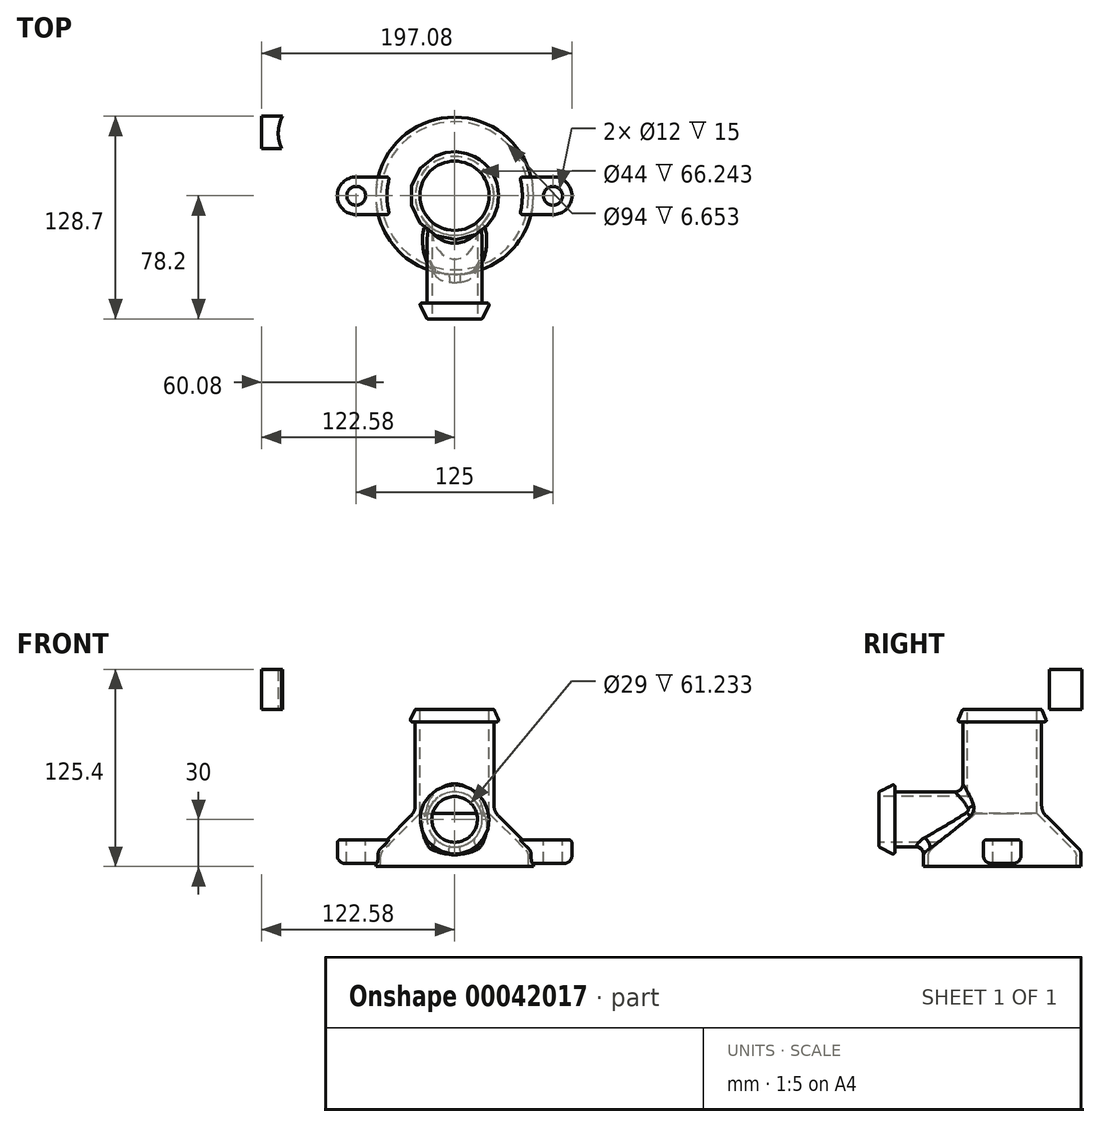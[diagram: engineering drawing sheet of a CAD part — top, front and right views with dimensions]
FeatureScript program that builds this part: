
annotation { "Feature Type Name" : "Feature", "Feature Type Description" : "" }
export const myFeature = defineFeature(function(context is Context, id is Id, definition is map)
    precondition{}
    {
        {
            var Q0;
            Q0=qCreatedBy(makeId("Front.planeOp"),FACE);
            var sketch = newSketch(context, id + "F0", { "sketchPlane" : qUnion([Q0])});
            skLineSegment(sketch, "E0", {"start": v(0, 100) * mm, "end": v(0, 0) * mm});
            skLineSegment(sketch, "E1", {"start": v(0, 0) * mm, "end": v(50, 0) * mm});
            skLineSegment(sketch, "E2", {"start": v(50, 0) * mm, "end": v(50, 10) * mm});
            skLineSegment(sketch, "E3", {"start": v(50, 10) * mm, "end": v(25, 35) * mm});
            skLineSegment(sketch, "E4", {"start": v(25, 35) * mm, "end": v(25, 92) * mm});
            skLineSegment(sketch, "E5", {"start": v(25, 92) * mm, "end": v(28.5, 92) * mm});
            skLineSegment(sketch, "E6", {"start": v(28.5, 92) * mm, "end": v(25, 100) * mm});
            skLineSegment(sketch, "E7", {"start": v(25, 100) * mm, "end": v(0, 100) * mm});
            skLineSegment(sketch, "E8", {"start": v(25, 100) * mm, "end": v(25, 92) * mm});
            skSolve(sketch);
        }
        {
            var Q0;
            Q0=qCreatedBy(makeId("Right.planeOp"),FACE);
            var sketch = newSketch(context, id + "F1", { "sketchPlane" : qUnion([Q0])});
            skLineSegment(sketch, "E9", {"start": v(0, 0) * mm, "end": v(96.43, 0) * mm, "construction": true});
            skLineSegment(sketch, "E10", {"start": v(0, 0) * mm, "end": v(0, 117.17) * mm, "construction": true});
            skLineSegment(sketch, "E11", {"start": v(0, 47.5) * mm, "end": v(-68.2, 47.5) * mm});
            skLineSegment(sketch, "E12", {"start": v(-68.2, 47.5) * mm, "end": v(-68.2, 52.5) * mm});
            skLineSegment(sketch, "E13", {"start": v(-68.2, 52.5) * mm, "end": v(-78.2, 47.5) * mm});
            skLineSegment(sketch, "E14", {"start": v(-78.2, 47.5) * mm, "end": v(-78.2, 30) * mm});
            skLineSegment(sketch, "E15", {"start": v(-78.2, 30) * mm, "end": v(0, 30) * mm});
            skLineSegment(sketch, "E16", {"start": v(0, 30) * mm, "end": v(0, 47.5) * mm});
            skLineSegment(sketch, "E17", {"start": v(-68.2, 47.5) * mm, "end": v(-78.2, 47.5) * mm});
            skLineSegment(sketch, "E18", {"start": v(0, 30) * mm, "end": v(-77.9, 30) * mm, "construction": true});
            skSolve(sketch);
        }
        {
            var Q0;
            Q0=makeQuery(id+"F0.imprint","IMPRINT",FACE,{"disambiguationData":[TD([[makeQuery(id+"F0.imprint","IMPRINT",EDGE,{"derivedFrom":sQuery(id+"F0.wireOp",EDGE,"E0")}),1.0]])]});
            var Q1;
            Q1=sQuery(id+"F0.wireOp",EDGE,"E6");
            var Q2;
            Q2=sQuery(id+"F0.wireOp",EDGE,"E5");
            var Q3;
            Q3=sQuery(id+"F0.wireOp",EDGE,"E4");
            var Q4;
            Q4=sQuery(id+"F0.wireOp",EDGE,"E3");
            var Q5;
            Q5=sQuery(id+"F0.wireOp",EDGE,"E2");
            var Q6;
            Q6=sQuery(id+"F0.wireOp",EDGE,"E0");
            revolve(context, id + "F2", {"entities" : qUnion([Q0]), "surfaceEntities" : qUnion([Q1, Q2, Q3, Q4, Q5]), "axis" : qUnion([Q6]), "revolveType" : RevolveType.FULL});
        }
        {
            var Q0;
            Q0=makeQuery(id+"F1.imprint","IMPRINT",FACE,{"disambiguationData":[TD([[makeQuery(id+"F1.imprint","IMPRINT",EDGE,{"derivedFrom":sQuery(id+"F1.wireOp",EDGE,"E11")}),1.0]])]});
            var Q1;
            Q1=sQuery(id+"F1.wireOp",EDGE,"E15");
            revolve(context, id + "F3", {"operationType" : NewBodyOperationType.ADD, "entities" : qUnion([Q0]), "axis" : qUnion([Q1]), "revolveType" : RevolveType.FULL});
        }
        {
            var Q0;
            Q0=makeQuery(id+"F2.opRevolve","SWEPT_FACE",FACE,{"disambiguationData":[OSD([sQuery(id+"F0.wireOp",EDGE,"E7")])]});
            var Q1;
            Q1=makeQuery(id+"F2.opRevolve","SWEPT_FACE",FACE,{"disambiguationData":[OSD([sQuery(id+"F0.wireOp",EDGE,"E1")])]});
            var Q2;
            Q2=makeQuery(id+"F3.opRevolve","SWEPT_FACE",FACE,{"disambiguationData":[OSD([sQuery(id+"F1.wireOp",EDGE,"E14")])]});
            shell(context, id + "F4", {"entities" : qUnion([Q0, Q1, Q2]), "thickness" : 3 * mm});
        }
        {
            var Q0;
            Q0=makeQuery(id+"F0.imprint","IMPRINT",FACE,{"disambiguationData":[TD([[makeQuery(id+"F0.imprint","IMPRINT",EDGE,{"derivedFrom":sQuery(id+"F0.wireOp",EDGE,"E5")}),1.0]])]});
            var Q1;
            Q1=makeQuery(id+"F4.opShell","OFFSET_FACE",FACE,{"disambiguationData":[OSD([sQuery(id+"F0.wireOp",EDGE,"E4"),sQuery(id+"F0.wireOp",EDGE,"E8")])]});
            revolve(context, id + "F5", {"operationType" : NewBodyOperationType.ADD, "entities" : qUnion([Q0]), "axis" : qUnion([Q1]), "revolveType" : RevolveType.FULL});
        }
        {
            var Q0;
            Q0=makeQuery(id+"F1.imprint","IMPRINT",FACE,{"disambiguationData":[TD([[makeQuery(id+"F1.imprint","IMPRINT",EDGE,{"derivedFrom":sQuery(id+"F1.wireOp",EDGE,"E12")}),1.0]])]});
            var Q1;
            Q1=makeQuery(id+"F3.opRevolve","SWEPT_FACE",FACE,{"disambiguationData":[OSD([sQuery(id+"F1.wireOp",EDGE,"E11"),sQuery(id+"F1.wireOp",EDGE,"E17")])]});
            revolve(context, id + "F6", {"operationType" : NewBodyOperationType.ADD, "entities" : qUnion([Q0]), "axis" : qUnion([Q1]), "revolveType" : RevolveType.FULL});
        }
        {
            var Q0;
            Q0=makeQuery(id+"F2.opRevolve","SWEPT_FACE",FACE,{"disambiguationData":[OSD([sQuery(id+"F0.wireOp",EDGE,"E1")])]});
            cPlane(context, id + "F7", {"entities" : qUnion([Q0]), "cplaneType" : CPlaneType.OFFSET, "offset" : 17 * mm, "oppositeDirection" : true, "width" : 152.4 * mm, "height" : 152.4 * mm});
        }
        {
            var Q0;
            Q0=qCreatedBy(id+"F7.planeOp",FACE);
            var sketch = newSketch(context, id + "F8", { "sketchPlane" : qUnion([Q0])});
            skLineSegment(sketch, "E19", {"start": v(0, -67.56) * mm, "end": v(0, 0) * mm, "construction": true});
            skLineSegment(sketch, "E20", {"start": v(0, 0) * mm, "end": v(-100, 0) * mm, "construction": true});
            skLineSegment(sketch, "E21", {"start": v(-50, 0) * mm, "end": v(-50, -12) * mm});
            skLineSegment(sketch, "E22", {"start": v(-50, -12) * mm, "end": v(-62.5, -12) * mm});
            skLineSegment(sketch, "E23", {"start": v(-74.5, 0) * mm, "end": v(-74.5, 0) * mm});
            skPoint(sketch, "E24.visualSharp", {"position": v(-74.5, -12) * mm});
            skArc(sketch, "E24.filletArc", {"start": v(-74.5, 0) * mm, "mid": v(-70.99, -8.49) * mm, "end": v(-62.5, -12) * mm});
            skCircle(sketch, "E25", {"center": v(-62.5, 0) * mm, "radius": 6 * mm});
            skLineSegment(sketch, "E26.0.MirrorCS", {"start": v(-50, 12) * mm, "end": v(-62.5, 12) * mm});
            skLineSegment(sketch, "E26.1.MirrorCS", {"start": v(-50, 0) * mm, "end": v(-50, 12) * mm});
            skArc(sketch, "E26.2.MirrorCS", {"start": v(-74.5, 0) * mm, "mid": v(-70.99, 8.49) * mm, "end": v(-62.5, 12) * mm});
            skSolve(sketch);
        }
        {
            var Q0;
            Q0=qSketchRegion(id+"F8",true);
            extrude(context, id + "F9", {"entities" : qUnion([Q0]), "operationType" : NewBodyOperationType.ADD, "depth" : 15 * mm});
        }
        {
            var Q0;
            Q0=makeQuery(id+"F9.opExtrude","SWEPT_FACE",FACE,{"disambiguationData":[OSD([sQuery(id+"F8.wireOp",EDGE,"E21"),sQuery(id+"F8.wireOp",EDGE,"E26.1.MirrorCS")])]});
            extrude(context, id + "F10", {"entities" : qUnion([Q0]), "operationType" : NewBodyOperationType.ADD, "endBound" : BoundingType.UP_TO_NEXT, "depth" : 25.4 * mm});
        }
        {
            var Q0;
            Q0=makeQuery(id+"F5.opRevolve","SWEPT_FACE",FACE,{"disambiguationData":[OSD([sQuery(id+"F0.wireOp",EDGE,"E6")])]});
            var Q1;
            Q1=makeQuery(id+"F6.opRevolve","SWEPT_FACE",FACE,{"disambiguationData":[OSD([sQuery(id+"F1.wireOp",EDGE,"E13")])]});
            var Q2;
            Q2=makeQuery(id+"F6.opRevolve","SWEPT_FACE",FACE,{"disambiguationData":[OSD([sQuery(id+"F1.wireOp",EDGE,"E12")])]});
            var Q3;
            Q3=makeQuery(id+"F5.opRevolve","SWEPT_FACE",FACE,{"disambiguationData":[OSD([sQuery(id+"F0.wireOp",EDGE,"E5")])]});
            fillet(context, id + "F11", {"entities" : qUnion([Q0, Q1, Q2, Q3]), "radius" : 1 * mm, "tangentPropagation" : true, "allowEdgeOverflow" : false});
        }
        {
            var Q0;
            Q0=makeQuery(id+"F2.opRevolve","SWEPT_FACE",FACE,{"disambiguationData":[OSD([sQuery(id+"F0.wireOp",EDGE,"E7")])]});
            var sketch = newSketch(context, id + "F12", { "sketchPlane" : qUnion([Q0])});
            skLineSegment(sketch, "E27.bottom", {"start": v(-122.58, 50.5) * mm, "end": v(-53.18, 50.5) * mm});
            skLineSegment(sketch, "E27.top", {"start": v(-122.58, 29.9) * mm, "end": v(-53.18, 29.9) * mm});
            skLineSegment(sketch, "E27.left", {"start": v(-122.58, 50.5) * mm, "end": v(-122.58, 29.9) * mm});
            skLineSegment(sketch, "E27.right", {"start": v(-53.18, 50.5) * mm, "end": v(-53.18, 29.9) * mm});
            skCircle(sketch, "E28", {"center": v(-88.45, 39.78) * mm, "radius": 23.54 * mm});
            skCircle(sketch, "E29", {"center": v(-88.45, 39.78) * mm, "radius": 14.73 * mm});
            skSolve(sketch);
        }
        {
            var Q0;
            Q0=makeQuery(id+"F17.opPattern","SPLIT",EDGE,{"disambiguationData":[OD(1.0)],"derivedFrom":makeQuery(id+"F2.opRevolve","SWEPT_EDGE",EDGE,{"disambiguationData":[OSD([sQuery(id+"F0.wireOp",EDGE,"E2"),sQuery(id+"F0.wireOp",EDGE,"E3")])]})});
            var Q1;
            Q1=makeQuery(id+"F17.opPattern","SPLIT",EDGE,{"disambiguationData":[OD(0.0)],"derivedFrom":makeQuery(id+"F2.opRevolve","SWEPT_EDGE",EDGE,{"disambiguationData":[OSD([sQuery(id+"F0.wireOp",EDGE,"E2"),sQuery(id+"F0.wireOp",EDGE,"E3")])]})});
            fillet(context, id + "F13", {"entities" : qUnion([Q0, Q1]), "radius" : 5 * mm, "allowEdgeOverflow" : false});
        }
        {
            var Q0;
            {var subQ0=sQuery(id+"F8.wireOp",EDGE,"E26.1.MirrorCS");var subQ1=sQuery(id+"F8.wireOp",EDGE,"E26.0.MirrorCS");Q0=makeQuery(id+"F10.boolean.opBoolean","MERGE",EDGE,{"derivedFrom":[makeQuery(id+"F9.opExtrude","CAP_EDGE",EDGE,{"disambiguationData":[OSD([subQ1])],"isStart":true}),makeQuery(id+"F10.opExtrude","SWEPT_EDGE",EDGE,{"disambiguationData":[OSD([subQ1,subQ0]),TDD([makeQuery(id+"F9.opExtrude","CAP_VERTEX",VERTEX,{"disambiguationData":[OSD([subQ1,subQ0])],"isStart":true})])]})]});}
            var Q1;
            {var subQ0=sQuery(id+"F8.wireOp",EDGE,"E26.1.MirrorCS");var subQ1=sQuery(id+"F8.wireOp",EDGE,"E21");Q1=makeQuery(id+"F10.opExtrude","CAP_EDGE",EDGE,{"disambiguationData":[OSD([subQ1,subQ0]),TDD([makeQuery(id+"F9.opExtrude","CAP_EDGE",EDGE,{"disambiguationData":[OSD([subQ1,subQ0])],"isStart":true})])],"isStart":false});}
            var Q2;
            Q2=makeQuery(id+"F10.opExtrude","CAP_EDGE",EDGE,{"disambiguationData":[OSD([sQuery(id+"F8.wireOp",EDGE,"E26.0.MirrorCS"),sQuery(id+"F8.wireOp",EDGE,"E26.1.MirrorCS")]),topologyDisambiguationEdgeConnected([makeQuery(id+"F2.opRevolve","SWEPT_FACE",FACE,{"disambiguationData":[OSD([sQuery(id+"F0.wireOp",EDGE,"E2")])]})])],"isStart":false});
            var Q3;
            Q3=makeQuery(id+"F10.opExtrude","CAP_EDGE",EDGE,{"disambiguationData":[OSD([sQuery(id+"F8.wireOp",EDGE,"E21"),sQuery(id+"F8.wireOp",EDGE,"E22")]),topologyDisambiguationEdgeConnected([makeQuery(id+"F2.opRevolve","SWEPT_FACE",FACE,{"disambiguationData":[OSD([sQuery(id+"F0.wireOp",EDGE,"E2")])]})])],"isStart":false});
            fillet(context, id + "F14", {"entities" : qUnion([Q0, Q1, Q2, Q3]), "radius" : 2 * mm, "tangentPropagation" : true, "allowEdgeOverflow" : false});
        }
        {
            var Q0;
            Q0=makeQuery(id+"F2.opRevolve","SWEPT_EDGE",EDGE,{"disambiguationData":[OSD([sQuery(id+"F0.wireOp",EDGE,"E3"),sQuery(id+"F0.wireOp",EDGE,"E4")])]});
            fillet(context, id + "F15", {"entities" : qUnion([Q0]), "radius" : 10 * mm, "tangentPropagation" : true, "allowEdgeOverflow" : false});
        }
        {
            var Q0;
            Q0=makeQuery(id+"F3.boolean.opBoolean","INTERSECT",EDGE,{"derivedFrom":[makeQuery(id+"F2.opRevolve","SWEPT_FACE",FACE,{"disambiguationData":[OSD([sQuery(id+"F0.wireOp",EDGE,"E3")])]}),makeQuery(id+"F3.opRevolve","SWEPT_FACE",FACE,{"disambiguationData":[OSD([sQuery(id+"F1.wireOp",EDGE,"E11"),sQuery(id+"F1.wireOp",EDGE,"E17")])]})]});
            var Q1;
            Q1=makeQuery(id+"F3.boolean.opBoolean","INTERSECT",EDGE,{"derivedFrom":[makeQuery(id+"F2.opRevolve","SWEPT_FACE",FACE,{"disambiguationData":[OSD([sQuery(id+"F0.wireOp",EDGE,"E4"),sQuery(id+"F0.wireOp",EDGE,"E8")])]}),makeQuery(id+"F3.opRevolve","SWEPT_FACE",FACE,{"disambiguationData":[OSD([sQuery(id+"F1.wireOp",EDGE,"E11"),sQuery(id+"F1.wireOp",EDGE,"E17")])]})]});
            fillet(context, id + "F16", {"entities" : qUnion([Q0, Q1]), "radius" : 5 * mm, "tangentPropagation" : true, "allowEdgeOverflow" : false});
        }
        {
            var Q0;
            Q0=makeQuery(id+"F9.opExtrude","SWEPT_BODY",BODY,{"disambiguationData":[OSD([sQuery(id+"F8.wireOp",EDGE,"E21"),sQuery(id+"F8.wireOp",EDGE,"E22"),sQuery(id+"F8.wireOp",EDGE,"E24.filletArc"),sQuery(id+"F8.wireOp",EDGE,"E25"),sQuery(id+"F8.wireOp",EDGE,"E26.0.MirrorCS"),sQuery(id+"F8.wireOp",EDGE,"E26.1.MirrorCS"),sQuery(id+"F8.wireOp",EDGE,"E26.2.MirrorCS")])]});
            var Q1;
            {var subQ0=sQuery(id+"F8.wireOp",EDGE,"E22");Q1=makeQuery(id+"F10.boolean.opBoolean","MERGE",FACE,{"derivedFrom":[makeQuery(id+"F9.opExtrude","SWEPT_FACE",FACE,{"disambiguationData":[OSD([subQ0])]}),makeQuery(id+"F10.opExtrude","SWEPT_FACE",FACE,{"disambiguationData":[OSD([sQuery(id+"F8.wireOp",EDGE,"E21"),subQ0])]})]});}
            var Q2;
            {var subQ0=sQuery(id+"F8.wireOp",EDGE,"E26.1.MirrorCS");var subQ1=sQuery(id+"F8.wireOp",EDGE,"E21");Q2=makeQuery(id+"F10.boolean.opBoolean","MERGE",FACE,{"derivedFrom":[makeQuery(id+"F9.opExtrude","CAP_FACE",FACE,{"disambiguationData":[OSD([subQ1,sQuery(id+"F8.wireOp",EDGE,"E22"),sQuery(id+"F8.wireOp",EDGE,"E24.filletArc"),sQuery(id+"F8.wireOp",EDGE,"E25"),sQuery(id+"F8.wireOp",EDGE,"E26.0.MirrorCS"),subQ0,sQuery(id+"F8.wireOp",EDGE,"E26.2.MirrorCS")])],"isStart":true}),makeQuery(id+"F10.opExtrude","SWEPT_FACE",FACE,{"disambiguationData":[OSD([subQ1,subQ0]),TDD([makeQuery(id+"F9.opExtrude","CAP_EDGE",EDGE,{"disambiguationData":[OSD([subQ1,subQ0])],"isStart":true})])]})]});}
            var Q3;
            Q3=makeQuery(id+"F9.opExtrude","SWEPT_FACE",FACE,{"disambiguationData":[OSD([sQuery(id+"F8.wireOp",EDGE,"E24.filletArc"),sQuery(id+"F8.wireOp",EDGE,"E26.2.MirrorCS")])]});
            var Q4;
            {var subQ0=sQuery(id+"F8.wireOp",EDGE,"E26.1.MirrorCS");var subQ1=sQuery(id+"F8.wireOp",EDGE,"E21");var subQ2=makeQuery(id+"F9.opExtrude","CAP_EDGE",EDGE,{"disambiguationData":[OSD([subQ1,subQ0])],"isStart":false});Q4=makeQuery(id+"F10.boolean.opBoolean","MERGE",FACE,{"derivedFrom":[makeQuery(id+"F9.opExtrude","CAP_FACE",FACE,{"disambiguationData":[OSD([subQ1,sQuery(id+"F8.wireOp",EDGE,"E22"),sQuery(id+"F8.wireOp",EDGE,"E24.filletArc"),sQuery(id+"F8.wireOp",EDGE,"E25"),sQuery(id+"F8.wireOp",EDGE,"E26.0.MirrorCS"),subQ0,sQuery(id+"F8.wireOp",EDGE,"E26.2.MirrorCS")])],"isStart":false}),makeQuery(id+"F10.opExtrude","SWEPT_FACE",FACE,{"disambiguationData":[OSD([subQ1,subQ0]),TDD([subQ2]),OD(0.0)]}),makeQuery(id+"F10.opExtrude","SWEPT_FACE",FACE,{"disambiguationData":[OSD([subQ1,subQ0]),TDD([subQ2]),OD(1.0)]})]});}
            var Q5;
            {var subQ0=sQuery(id+"F8.wireOp",EDGE,"E26.0.MirrorCS");Q5=makeQuery(id+"F10.boolean.opBoolean","MERGE",FACE,{"derivedFrom":[makeQuery(id+"F9.opExtrude","SWEPT_FACE",FACE,{"disambiguationData":[OSD([subQ0])]}),makeQuery(id+"F10.opExtrude","SWEPT_FACE",FACE,{"disambiguationData":[OSD([subQ0,sQuery(id+"F8.wireOp",EDGE,"E26.1.MirrorCS")])]})]});}
            var Q6;
            Q6=makeQuery(id+"F9.opExtrude","SWEPT_FACE",FACE,{"disambiguationData":[OSD([sQuery(id+"F8.wireOp",EDGE,"E25")])]});
            var Q7;
            Q7=makeQuery(id+"F14.opFillet","BLEND_FACE",FACE,{"disambiguationData":[OSD([sQuery(id+"F0.wireOp",EDGE,"E2"),sQuery(id+"F8.wireOp",EDGE,"E26.0.MirrorCS"),sQuery(id+"F8.wireOp",EDGE,"E26.1.MirrorCS")])]});
            var Q8;
            Q8=makeQuery(id+"F14.opFillet","BLEND_FACE",FACE,{"disambiguationData":[OSD([sQuery(id+"F0.wireOp",EDGE,"E3"),sQuery(id+"F8.wireOp",EDGE,"E21"),sQuery(id+"F8.wireOp",EDGE,"E26.1.MirrorCS")])]});
            var Q9;
            Q9=makeQuery(id+"F14.opFillet","BLEND_FACE",FACE,{"disambiguationData":[OSD([sQuery(id+"F0.wireOp",EDGE,"E3"),sQuery(id+"F8.wireOp",EDGE,"E26.0.MirrorCS"),sQuery(id+"F8.wireOp",EDGE,"E26.1.MirrorCS")])]});
            var Q10;
            Q10=makeQuery(id+"F14.opFillet","BLEND_FACE",FACE,{"disambiguationData":[OSD([sQuery(id+"F0.wireOp",EDGE,"E3"),sQuery(id+"F8.wireOp",EDGE,"E21"),sQuery(id+"F8.wireOp",EDGE,"E22"),sQuery(id+"F8.wireOp",EDGE,"E26.1.MirrorCS")])]});
            var Q11;
            Q11=makeQuery(id+"F14.opFillet","BLEND_FACE",FACE,{"disambiguationData":[OSD([sQuery(id+"F0.wireOp",EDGE,"E3"),sQuery(id+"F8.wireOp",EDGE,"E21"),sQuery(id+"F8.wireOp",EDGE,"E26.0.MirrorCS"),sQuery(id+"F8.wireOp",EDGE,"E26.1.MirrorCS")])]});
            var Q12;
            Q12=makeQuery(id+"F14.opFillet","BLEND_FACE",FACE,{"disambiguationData":[OSD([sQuery(id+"F0.wireOp",EDGE,"E2"),sQuery(id+"F8.wireOp",EDGE,"E21"),sQuery(id+"F8.wireOp",EDGE,"E22")])]});
            var Q13;
            Q13=makeQuery(id+"F14.opFillet","BLEND_FACE",FACE,{"disambiguationData":[OSD([sQuery(id+"F0.wireOp",EDGE,"E3"),sQuery(id+"F8.wireOp",EDGE,"E21"),sQuery(id+"F8.wireOp",EDGE,"E22")])]});
            var Q14;
            Q14=makeQuery(id+"F14.opFillet","BLEND_FACE",FACE,{"disambiguationData":[OSD([sQuery(id+"F8.wireOp",EDGE,"E24.filletArc"),sQuery(id+"F8.wireOp",EDGE,"E26.2.MirrorCS")])]});
            var Q15;
            Q15=makeQuery(id+"F14.opFillet","BLEND_FACE",FACE,{"disambiguationData":[OSD([sQuery(id+"F8.wireOp",EDGE,"E26.0.MirrorCS"),sQuery(id+"F8.wireOp",EDGE,"E26.1.MirrorCS")])]});
            var Q16;
            Q16=makeQuery(id+"F14.opFillet","BLEND_FACE",FACE,{"disambiguationData":[OSD([sQuery(id+"F8.wireOp",EDGE,"E21"),sQuery(id+"F8.wireOp",EDGE,"E22")])]});
            var Q17;
            Q17=makeQuery(id+"F14.opFillet","BLEND_FACE",FACE,{"disambiguationData":[OSD([sQuery(id+"F0.wireOp",EDGE,"E2"),sQuery(id+"F0.wireOp",EDGE,"E3"),sQuery(id+"F8.wireOp",EDGE,"E26.0.MirrorCS"),sQuery(id+"F8.wireOp",EDGE,"E26.1.MirrorCS")])]});
            var Q18;
            Q18=makeQuery(id+"F14.opFillet","BLEND_FACE",FACE,{"disambiguationData":[OSD([sQuery(id+"F0.wireOp",EDGE,"E2"),sQuery(id+"F0.wireOp",EDGE,"E3"),sQuery(id+"F8.wireOp",EDGE,"E21"),sQuery(id+"F8.wireOp",EDGE,"E22")])]});
            var Q19;
            Q19=makeQuery(id+"F4.opShell","OFFSET_FACE",FACE,{"disambiguationData":[OSD([sQuery(id+"F0.wireOp",EDGE,"E4")])]});
            circularPattern(context, id + "F17", {"faces" : qUnion([Q1, Q2, Q3, Q4, Q5, Q6, Q7, Q8, Q9, Q10, Q11, Q12, Q13, Q14, Q15, Q16, Q17, Q18]), "axis" : qUnion([Q19]), "angle" : 360 * degree, "instanceCount" : 2, "equalSpace" : true, "patternType" : PatternType.FACE});
        }
        {
            var Q0;
            {var subQ5=sQuery(id+"F12.wireOp",EDGE,"E27.right");Q0=makeQuery(id+"F12.imprint","IMPRINT",FACE,{"disambiguationData":[TD([[makeQuery(id+"F12.imprint","IMPRINT",EDGE,{"derivedFrom":subQ5}),-1.0]])]});}
            var Q1;
            {var subQ3=sQuery(id+"F12.wireOp",EDGE,"E27.bottom");var subQ5=sQuery(id+"F12.wireOp",EDGE,"E28");var subQ7=makeQuery(id+"F12.imprint","INTERSECT",VERTEX,{"disambiguationData":[OD(1.0)],"derivedFrom":[subQ3,subQ5]});Q1=makeQuery(id+"F12.imprint","IMPRINT",FACE,{"disambiguationData":[TD([[makeQuery(id+"F12.imprint","IMPRINT",EDGE,{"disambiguationData":[TD([[subQ7,1.0]])],"derivedFrom":subQ3}),-1.0]])]});}
            var Q2;
            {var subQ1=sQuery(id+"F12.wireOp",EDGE,"E27.bottom");var subQ4=sQuery(id+"F12.wireOp",EDGE,"E28");var subQ6=makeQuery(id+"F12.imprint","INTERSECT",VERTEX,{"disambiguationData":[OD(0.0)],"derivedFrom":[subQ1,subQ4]});Q2=makeQuery(id+"F12.imprint","IMPRINT",FACE,{"disambiguationData":[TD([[makeQuery(id+"F12.imprint","IMPRINT",EDGE,{"disambiguationData":[TD([[subQ6,-1.0]])],"derivedFrom":subQ1}),1.0]])]});}
            var Q3;
            {var subQ1=sQuery(id+"F12.wireOp",EDGE,"E27.top");var subQ4=sQuery(id+"F12.wireOp",EDGE,"E28");var subQ6=makeQuery(id+"F12.imprint","INTERSECT",VERTEX,{"disambiguationData":[OD(0.0)],"derivedFrom":[subQ1,subQ4]});Q3=makeQuery(id+"F12.imprint","IMPRINT",FACE,{"disambiguationData":[TD([[makeQuery(id+"F12.imprint","IMPRINT",EDGE,{"disambiguationData":[TD([[subQ6,-1.0]])],"derivedFrom":subQ1}),-1.0]])]});}
            extrude(context, id + "F18", {"entities" : qUnion([Q0, Q1, Q2, Q3]), "operationType" : NewBodyOperationType.ADD, "depth" : 25.4 * mm});
        }
        {
            var Q0;
            Q0=makeQuery(id+"F9.opExtrude","CAP_EDGE",EDGE,{"disambiguationData":[OSD([sQuery(id+"F8.wireOp",EDGE,"E24.filletArc"),sQuery(id+"F8.wireOp",EDGE,"E26.2.MirrorCS")])],"isStart":false});
            fillet(context, id + "F19", {"entities" : qUnion([Q0]), "radius" : 5.08 * mm, "tangentPropagation" : true, "allowEdgeOverflow" : false});
        }
        {
            var Q0;
            Q0=makeQuery(id+"F17.opPattern","COPY",EDGE,{"derivedFrom":makeQuery(id+"F9.opExtrude","CAP_EDGE",EDGE,{"disambiguationData":[OSD([sQuery(id+"F8.wireOp",EDGE,"E24.filletArc"),sQuery(id+"F8.wireOp",EDGE,"E26.2.MirrorCS")])],"isStart":false}),"instanceName":"1"});
            fillet(context, id + "F20", {"entities" : qUnion([Q0]), "radius" : 5.08 * mm, "tangentPropagation" : true, "allowEdgeOverflow" : false});
        }
        {
            var Q0;
            Q0=makeQuery(id+"F18.opExtrude","SWEPT_BODY",BODY,{"disambiguationData":[OSD([sQuery(id+"F12.wireOp",EDGE,"E27.bottom"),sQuery(id+"F12.wireOp",EDGE,"E27.top"),sQuery(id+"F12.wireOp",EDGE,"E27.right"),sQuery(id+"F12.wireOp",EDGE,"E28"),sQuery(id+"F12.wireOp",EDGE,"E29")])]});
            deleteBodies(context, id + "F23", {"entities" : qUnion([Q0])});
        }
        {
            var Q0;
            Q0=makeQuery(id+"F4.opShell","OFFSET_EDGE",EDGE,{"disambiguationData":[OSD([sQuery(id+"F0.wireOp",EDGE,"E2"),sQuery(id+"F0.wireOp",EDGE,"E3")])]});
            fillet(context, id + "F21", {"entities" : qUnion([Q0]), "radius" : 5.08 * mm, "tangentPropagation" : true, "allowEdgeOverflow" : false});
        }
    });
